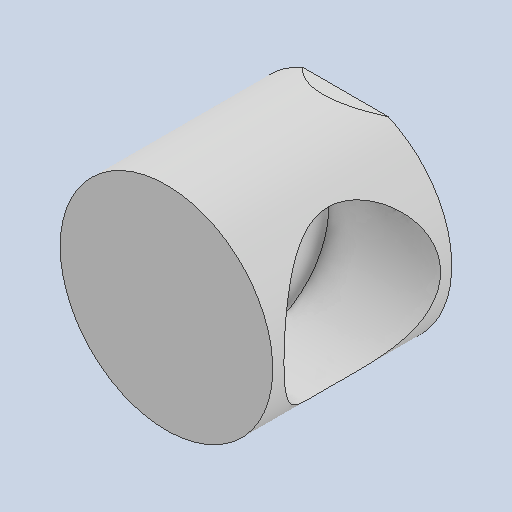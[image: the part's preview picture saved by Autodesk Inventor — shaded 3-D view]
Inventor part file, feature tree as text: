
AUTODESK INVENTOR PART (.ipt)
format: ipt  version: 2022 (Build 260153000, 153)  size: 114,176 bytes
history: native  units: in
note: dims shown in document units (in); Inventor stores cm internally (conversion verified against a paired STEP export)
features: extrude x1
ambient origin geometry x8: Origin, YZ Plane, XZ Plane, XY Plane, X Axis, Y Axis, Z Axis, Center Point
bodies: Solid1 (feature_tree)
feature tree (1):
  extrude  "Extrusion1"  [1 undecoded]
note: 1 required parameter value undecoded (feature->parameter linkage not recoverable at this tier; creation-order binding heuristic only, values carry confidence <= 0.55)
